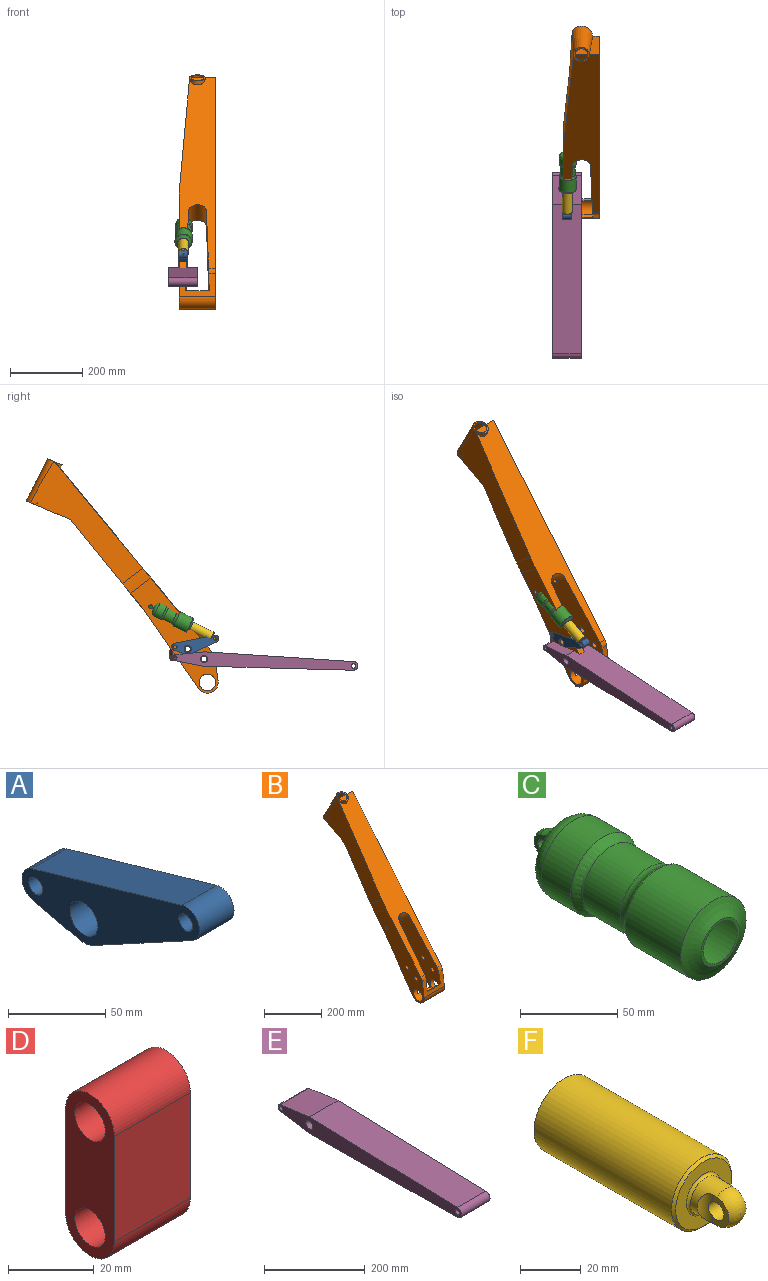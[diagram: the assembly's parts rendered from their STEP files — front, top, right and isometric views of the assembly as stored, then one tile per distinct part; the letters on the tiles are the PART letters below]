
ASSEMBLY  parts=6 mates=7
PART A: 11 faces, bbox 25x128.8x59.5 mm
  f0: plane 33.72x25mm, normal (0,0.23,-0.97), area 865.9mm2, adj f1,f8,f9,f10
  f1: cylinder r=10mm len=25mm, axis (-1,0,0), area 657.4mm2, adj f0,f2,f9,f10
  f2: plane 108.83x31.44mm, normal (0,0.28,0.96), area 2832mm2, adj f1,f3,f9,f10
  f3: cylinder r=10mm len=25mm, axis (-1,0,0), area 731.3mm2, adj f2,f4,f9,f10
  f4: plane 71.58x38.88mm, normal (0,-0.48,-0.88), area 2036.6mm2, adj f3,f8,f9,f10
  f5: cylinder r=5mm len=25mm, axis (-1,0,0), area 785.4mm2, adj f9,f10
  f6: cylinder r=5mm len=25mm, axis (-1,0,0), area 785.4mm2, adj f9,f10
  f7: cylinder r=10mm len=25mm, axis (-1,0,0), area 1570.8mm2, adj f9,f10
  f8: cylinder r=15mm len=25mm, axis (-1,0,0), area 273.1mm2, adj f0,f4,f9,f10
  f9: plane 128.83x59.49mm, normal (1,0,0), area 3186.4mm2, adj f0,f1,f2,f3,f4,f5,f6,f7
  f10: plane 128.83x59.49mm, normal (-1,0,0), area 3186.4mm2, adj f0,f1,f2,f3,f4,f5,f6,f7
PART B: 38 faces, bbox 100x532.4x649.5 mm
  f0: cylinder r=30mm len=19.18mm, axis (-1,0,0), area 312.4mm2, adj f16,f18,f23,f34
  f1: plane 214.41x148.51mm, normal (0,0.82,-0.57), area 5543.3mm2, adj f15,f20,f23,f34
  f2: cylinder r=5.5mm len=25.6mm, axis (-1,0,0), area 866.9mm2, adj f22,f33,f36
  f3: cylinder r=8mm len=19.37mm, axis (-1,0,0), area 962mm2, adj f23,f34
  f4: cylinder r=8mm len=20.78mm, axis (-1,0,0), area 1032.8mm2, adj f23,f34
  f5: cone r=21.79mm half-angle=4deg, axis (0,0.39,-0.92), area 0.5mm2, adj f13,f19,f31
  f6: cone r=17.5mm half-angle=4deg, axis (0,0.39,-0.92), area 8236mm2, adj f7,f10,f26
  f7: cylinder r=17.5mm len=35mm, axis (0,-0.39,0.92), area 274.9mm2, adj f6,f13,f26
  f8: cone r=21.79mm half-angle=4deg, axis (0,0.39,-0.92), area 9229.3mm2, adj f9,f13,f25,f31
  f9: plane 122.42x82.66mm, normal (0,0.39,-0.92), area 8504.1mm2, adj f8,f10,f20,f23,f25,f26,f31
  f10: cylinder r=26mm len=52mm, axis (0,-0.39,0.92), area 408.4mm2, adj f6,f9,f26
  f11: cone r=17.5mm half-angle=4deg, axis (0,0.39,-0.92), area 95.7mm2, adj f12,f27
  f12: cylinder r=17.5mm len=35mm, axis (0,-0.39,0.92), area 225.2mm2, adj f11,f13,f27
  f13: plane 43.59x40.12mm, normal (0,-0.39,0.92), area 529.9mm2, adj f5,f7,f8,f12,f14
  f14: cone r=21.79mm half-angle=4deg, axis (0,0.39,-0.92), area 514.9mm2, adj f13,f18
  f15: cylinder r=30mm len=100mm, axis (-1,0,0), area 7967.9mm2, adj f1,f16,f21,f22,f23,f32,f33,f34
  f16: plane 100x64.62mm, normal (0,-0.99,0.14), area 3404.8mm2, adj f0,f15,f17,f22,f23,f33,f34,f35
  f17: cylinder r=30mm len=19.18mm, axis (-1,0,0), area 312.4mm2, adj f16,f18,f22,f33
  f18: plane 527.24x436.82mm, normal (0,-0.77,0.64), area 49615.9mm2, adj f0,f14,f17,f19,f22,f23,f25,f31
  f19: plane 1.05x0.45mm, normal (0,0.92,0.39), area 0mm2, adj f5,f18,f31
  f20: plane 253.94x206.83mm, normal (0,0.78,-0.63), area 29623mm2, adj f1,f9,f21,f22,f23,f31,f33,f34
  f21: plane 214.41x148.51mm, normal (0,0.82,-0.57), area 5543.3mm2, adj f15,f20,f22,f33
  f22: plane 319.02x243.24mm, normal (-1,0,0), area 24732.2mm2, adj f2,f15,f16,f17,f18,f20,f21,f24
  f23: plane 641x503.89mm, normal (1,0,0), area 55134.4mm2, adj f0,f1,f3,f4,f9,f15,f16,f18
  f24: cylinder r=23mm len=100mm, axis (-1,0,0), area 9815.1mm2, adj f22,f23,f32,f33,f34,f35
  f25: plane 119.88x50.89mm, normal (0,0.92,0.39), area 3073.9mm2, adj f8,f9,f18,f23
  f26: plane 119.88x52mm, normal (0,0.92,0.39), area 5665.1mm2, adj f6,f7,f9,f10,f27
  f27: plane 35x15.43mm, normal (0,-0.77,0.64), area 549.2mm2, adj f11,f12,f26
  f28: cylinder r=5.5mm len=25.6mm, axis (-1,0,0), area 866.9mm2, adj f23,f34,f36
  f29: cylinder r=8mm len=19.37mm, axis (-1,0,0), area 962mm2, adj f22,f33
  f30: cylinder r=8mm len=20.78mm, axis (-1,0,0), area 1032.8mm2, adj f22,f33
  f31: plane 337.79x311.6mm, normal (-1,0.04,0.06), area 29509.4mm2, adj f5,f8,f9,f18,f19,f20,f37
  f32: plane 65x5.61mm, normal (0,0.6,0.8), area 455mm2, adj f15,f24,f33,f34
  f33: plane 258.69x201.07mm, normal (1,-0.02,-0.02), area 19709.6mm2, adj f2,f15,f16,f17,f18,f20,f21,f24
  f34: plane 258.69x201.07mm, normal (-1,-0.02,-0.02), area 19709.6mm2, adj f0,f1,f3,f4,f15,f16,f18,f20
  f35: plane 65x8.94mm, normal (0,0.6,0.8), area 724.3mm2, adj f16,f24,f33,f34
  f36: cylinder r=25.01mm len=72.79mm, axis (0,0.8,-0.6), area 5435.1mm2, adj f2,f18,f20,f28,f33,f34
  f37: cylinder r=500mm len=79.21mm, axis (0,0.8,-0.6), area 2493.9mm2, adj f18,f20,f22,f31
PART C: 31 faces, bbox 47.5x132.6x47.5 mm
  f0: sphere r=7.5mm, area 140.4mm2, adj f1,f9,f12
  f1: revolved ~47.44x47.44mm, area 2424.7mm2, adj f0,f4,f9,f10,f11,f12,f13,f14
  f2: torus R=34.67mm, axis (0,1,0), area 1291.8mm2, adj f3,f8
  f3: plane 28x28mm, normal (0,-1,0), area 136.7mm2, adj f2,f18
  f4: cylinder r=23.72mm len=47.44mm, axis (0,1,0), area 3158.1mm2, adj f1,f5
  f5: revolved ~47.44x47.44mm, area 933mm2, adj f4,f6
  f6: cylinder r=20.72mm len=41.44mm, axis (0,1,0), area 3516.9mm2, adj f5,f7
  f7: revolved ~47.44x47.44mm, area 1097.9mm2, adj f6,f8
  f8: cylinder r=23.72mm len=47.44mm, axis (0,1,0), area 5961.8mm2, adj f2,f7
  f9: plane 17.71x10.64mm, normal (1,0,0), area 94.6mm2, adj f0,f1,f10,f15
  f10: cylinder r=2mm len=19.13mm, axis (0,0,1), area 58.8mm2, adj f1,f9,f11
  f11: plane 18.52x5.27mm, normal (0,1,0), area 69.1mm2, adj f1,f10
  f12: plane 17.28x10.34mm, normal (-1,0,0), area 86.7mm2, adj f0,f1,f14,f15
  f13: plane 17.87x4.76mm, normal (0,1,0), area 59.9mm2, adj f1,f14
  f14: cylinder r=2mm len=18.62mm, axis (0,0,1), area 57.3mm2, adj f1,f12,f13
  f15: cylinder r=3.5mm len=7.49mm, axis (-1,0,0), area 164.8mm2, adj f9,f12
  f16: sphere r=6.5mm, area 89.5mm2, adj f17,f24,f27
  f17: revolved ~45.44x45.44mm, area 2172.8mm2, adj f16,f19,f24,f25,f26,f27,f28,f29
  f18: torus R=34.67mm, axis (0,1,0), area 1299mm2, adj f3,f23
  f19: cylinder r=22.72mm len=45.44mm, axis (0,1,0), area 3024.9mm2, adj f17,f20
  f20: revolved ~45.44x45.44mm, area 885.5mm2, adj f19,f21
  f21: cylinder r=19.72mm len=39.44mm, axis (0,1,0), area 3347.2mm2, adj f20,f22
  f22: revolved ~45.44x45.44mm, area 1043.2mm2, adj f21,f23
  f23: cylinder r=22.72mm len=45.44mm, axis (0,1,0), area 5608.3mm2, adj f18,f22
  f24: plane 16.14x10.1mm, normal (-1,0,0), area 52mm2, adj f16,f17,f25,f30
  f25: cylinder r=3mm len=18.26mm, axis (0,0,1), area 81.5mm2, adj f17,f24,f26,f30
  f26: plane 17.39x4.79mm, normal (0,-1,0), area 58.8mm2, adj f17,f25
  f27: plane 15.8x9.87mm, normal (1,0,0), area 46.1mm2, adj f16,f17,f29,f30
  f28: plane 16.71x4.29mm, normal (0,-1,0), area 50.2mm2, adj f17,f29
  f29: cylinder r=3mm len=17.78mm, axis (0,0,1), area 79.4mm2, adj f17,f27,f28,f30
  f30: cylinder r=4.5mm len=9mm, axis (-1,0,0), area 155.3mm2, adj f24,f25,f27,f29
PART D: 8 faces, bbox 25x16x46 mm
  f0: plane 30x25mm, normal (0,1,0), area 750mm2, adj f1,f5,f6,f7
  f1: cylinder r=8mm len=25mm, axis (-1,0,0), area 628.3mm2, adj f0,f2,f6,f7
  f2: plane 30x25mm, normal (0,-1,0), area 750mm2, adj f1,f5,f6,f7
  f3: cylinder r=5mm len=25mm, axis (-1,0,0), area 785.4mm2, adj f6,f7
  f4: cylinder r=5mm len=25mm, axis (-1,0,0), area 785.4mm2, adj f6,f7
  f5: cylinder r=8mm len=25mm, axis (-1,0,0), area 628.3mm2, adj f0,f2,f6,f7
  f6: plane 46x16mm, normal (1,0,0), area 524mm2, adj f0,f1,f2,f3,f4,f5
  f7: plane 46x16mm, normal (-1,0,0), area 524mm2, adj f0,f1,f2,f3,f4,f5
PART E: 11 faces, bbox 80x514.9x40 mm
  f0: plane 81.41x80mm, normal (0,0.16,-0.99), area 6595.4mm2, adj f1,f8,f9,f10
  f1: cylinder r=8mm len=80mm, axis (-1,0,0), area 1822.3mm2, adj f0,f2,f9,f10
  f2: plane 81.68x80mm, normal (0,0.14,0.99), area 6595.5mm2, adj f1,f3,f9,f10
  f3: plane 414.62x80mm, normal (0,-0.03,1), area 33185.2mm2, adj f2,f4,f9,f10
  f4: cylinder r=12mm len=80mm, axis (-1,0,0), area 2978.9mm2, adj f3,f8,f9,f10
  f5: cylinder r=6mm len=80mm, axis (-1,0,0), area 3015.9mm2, adj f9,f10
  f6: cylinder r=10mm len=80mm, axis (-1,0,0), area 5026.5mm2, adj f9,f10
  f7: cylinder r=5mm len=80mm, axis (-1,0,0), area 2513.3mm2, adj f9,f10
  f8: plane 414.8x80mm, normal (0,-0.01,-1), area 33185.2mm2, adj f0,f4,f9,f10
  f9: plane 514.86x39.99mm, normal (1,0,0), area 15342mm2, adj f0,f1,f2,f3,f4,f5,f6,f7
  f10: plane 514.86x39.99mm, normal (-1,0,0), area 15342mm2, adj f0,f1,f2,f3,f4,f5,f6,f7
PART F: 12 faces, bbox 28x82x28 mm
  f0: cylinder r=7mm len=14mm, axis (0,1,0), area 228mm2, adj f1,f5,f6,f7,f8,f10
  f1: sphere r=7mm, area 175.9mm2, adj f0,f5,f8
  f2: plane 28x28mm, normal (0,1,0), area 615.8mm2, adj f3
  f3: cylinder r=14mm len=64mm, axis (0,1,0), area 5629.7mm2, adj f2,f9
  f4: plane 26x26mm, normal (0,-1,0), area 329.9mm2, adj f9,f10
  f5: plane 11.49x7.74mm, normal (-1,0,0), area 42.4mm2, adj f0,f1,f6,f11
  f6: cylinder r=4mm len=11.49mm, axis (0,0,1), area 42.1mm2, adj f0,f5,f11
  f7: cylinder r=4mm len=11.49mm, axis (0,0,1), area 48.3mm2, adj f0,f8
  f8: plane 11.49x9.74mm, normal (1,0,0), area 59.3mm2, adj f0,f1,f7,f11
  f9: cone r=14mm half-angle=45deg, axis (0,1,0), area 120mm2, adj f3,f4
  f10: torus R=8mm, axis (0,-1,0), area 72.7mm2, adj f0,f4
  f11: cylinder r=3.5mm len=8.29mm, axis (1,0,0), area 176.9mm2, adj f5,f6,f8
PLACE A rot(axis=(1,0,0),4.6deg) t=(-55.15,684.91,112.18)mm
PLACE B t=(-15.6,684.43,59.29)mm fixed
PLACE C rot(axis=(0.15,-0.96,-0.23),110.8deg) t=(-52.8,129.2,208.86)mm
PLACE D rot(axis=(0.01,0,1),113deg) t=(-629.4,-181.98,73.38)mm
PLACE E rot(axis=(1,0,0),2deg) t=(-55.86,684.16,83.88)mm
PLACE F rot(axis=(0.15,-0.96,-0.23),110.8deg) t=(-52.8,129.28,208.9)mm
MATE ball F.f11 <-> A.f3  axis (-0.32,-0.42,0.85) through (-55.15,-49.95,120.19)mm
MATE ball E.f1 <-> D.f4  axis (-1,0,0) through (-55.86,61.33,67.59)mm
MATE ball A.f1 <-> D.f1  axis (-1,0,0) through (-55.15,61.05,97.58)mm
MATE revolute B.f0 <-> E.f6  axis (-1,0,0) through (-55.86,-18.58,63.91)mm
MATE slider F.f0 <-> C.f2  axis (0.01,0.9,0.44) through (-54.31,17.22,153.55)mm
MATE revolute A.f7 <-> B.f4  axis (-1,0,0) through (-55.15,26.55,91.75)mm
MATE ball C.f15 <-> B.f2  axis (0.32,0.42,-0.85) through (-52.72,129.31,208.65)mm
